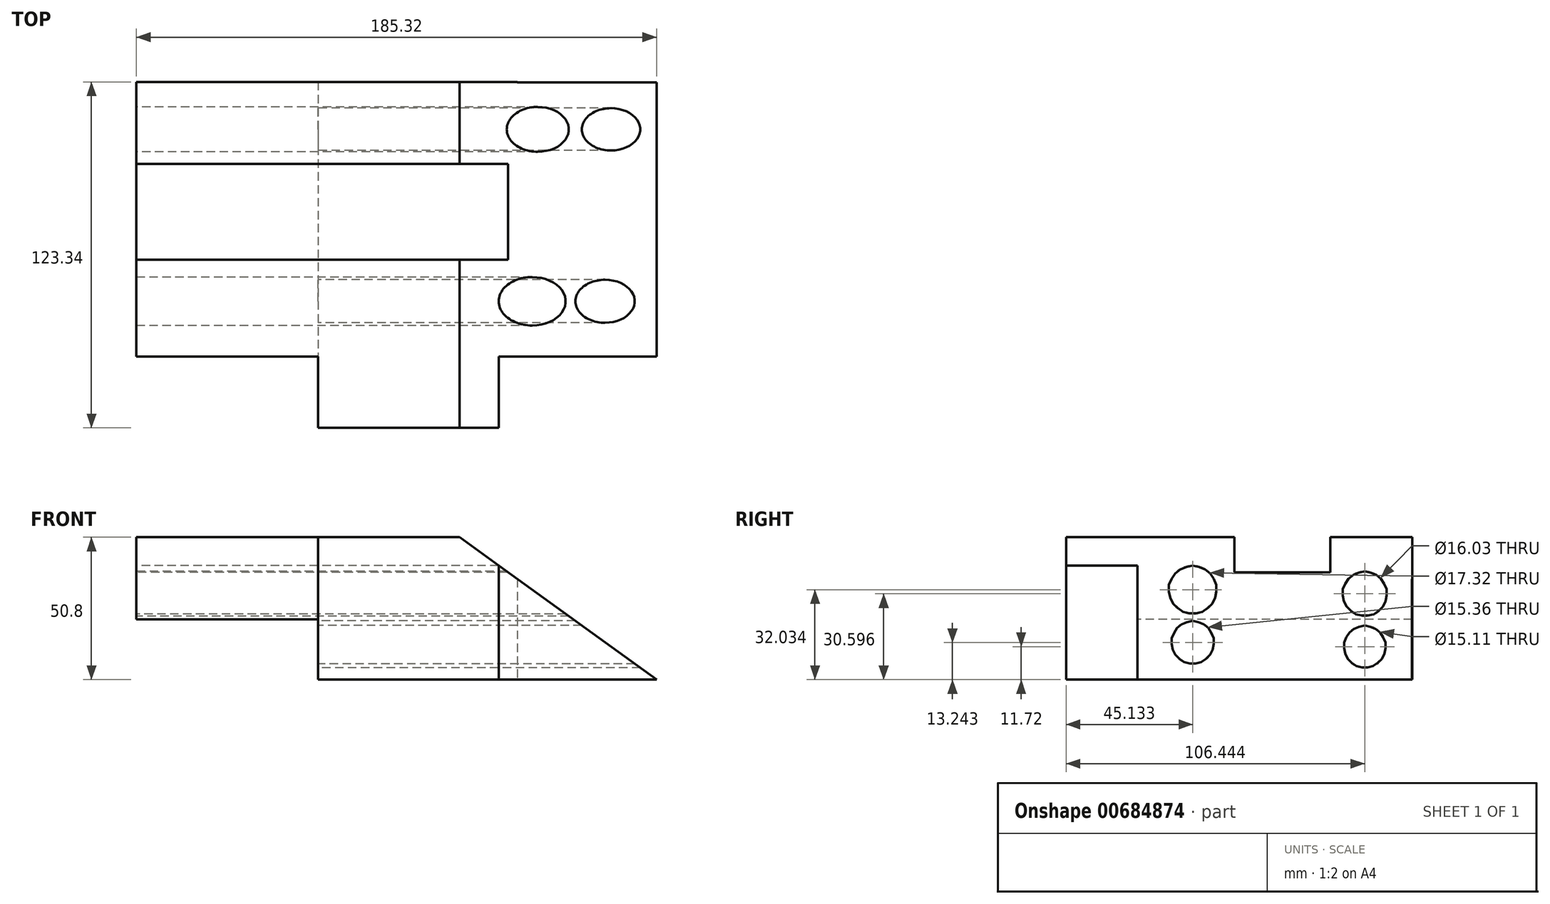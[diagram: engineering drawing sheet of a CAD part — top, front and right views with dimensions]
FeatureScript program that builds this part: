
annotation { "Feature Type Name" : "Feature", "Feature Type Description" : "" }
export const myFeature = defineFeature(function(context is Context, id is Id, definition is map)
    precondition{}
    {
        {
            var Q0;
            Q0=qCreatedBy(makeId("Top.planeOp"),FACE);
            var sketch = newSketch(context, id + "F0", { "sketchPlane" : qUnion([Q0])});
            skLineSegment(sketch, "E0.bottom", {"start": v(-58.71, -23.67) * mm, "end": v(125.79, -23.67) * mm});
            skLineSegment(sketch, "E0.top", {"start": v(-58.71, 74.27) * mm, "end": v(125.79, 74.27) * mm});
            skLineSegment(sketch, "E0.left", {"start": v(-58.71, -23.67) * mm, "end": v(-58.71, 74.27) * mm});
            skLineSegment(sketch, "E0.right", {"start": v(125.79, -23.67) * mm, "end": v(125.79, 74.27) * mm});
            skSolve(sketch);
        }
        {
            var Q0;
            Q0=makeQuery(id+"F0.imprint","IMPRINT",FACE,{"disambiguationData":[TD([[makeQuery(id+"F0.imprint","IMPRINT",EDGE,{"derivedFrom":sQuery(id+"F0.wireOp",EDGE,"E0.bottom")}),1.0]])]});
            extrude(context, id + "F1", {"entities" : qUnion([Q0]), "depth" : 50.8 * mm, "offsetDistance" : 25.4 * mm});
        }
        {
            var Q0;
            Q0=makeQuery(id+"F1.opExtrude","CAP_FACE",FACE,{"disambiguationData":[OSD([sQuery(id+"F0.wireOp",EDGE,"E0.bottom"),sQuery(id+"F0.wireOp",EDGE,"E0.top"),sQuery(id+"F0.wireOp",EDGE,"E0.left"),sQuery(id+"F0.wireOp",EDGE,"E0.right")])],"isStart":false});
            var sketch = newSketch(context, id + "F2", { "sketchPlane" : qUnion([Q0])});
            skLineSegment(sketch, "E1.bottom", {"start": v(125.79, -23.67) * mm, "end": v(77.04, -23.67) * mm});
            skLineSegment(sketch, "E1.top", {"start": v(125.79, 8.5) * mm, "end": v(77.04, 8.5) * mm});
            skLineSegment(sketch, "E1.left", {"start": v(125.79, -23.67) * mm, "end": v(125.79, 8.5) * mm});
            skLineSegment(sketch, "E1.right", {"start": v(77.04, -23.67) * mm, "end": v(77.04, 8.5) * mm});
            skSolve(sketch);
        }
        {
            var Q0;
            Q0 = qSketchRegion(id + "F2", true);
            extrude(context, id + "F3", {"entities" : qUnion([Q0]), "operationType" : NewBodyOperationType.REMOVE, "oppositeDirection" : true, "depth" : 51.82 * mm, "offsetDistance" : 25.4 * mm});
        }
        {
            var Q0;
            Q0=makeQuery(id+"F1.opExtrude","SWEPT_FACE",FACE,{"disambiguationData":[OSD([sQuery(id+"F0.wireOp",EDGE,"E0.bottom")])]});
            var sketch = newSketch(context, id + "F4", { "sketchPlane" : qUnion([Q0])});
            skLineSegment(sketch, "E2", {"start": v(56.37, 50.8) * mm, "end": v(126.6, 0) * mm});
            skLineSegment(sketch, "E3", {"start": v(126.6, 0) * mm, "end": v(54.95, 0) * mm});
            skLineSegment(sketch, "E4", {"start": v(54.95, 0) * mm, "end": v(56.37, 50.8) * mm});
            skSolve(sketch);
        }
        {
            var Q0;
            Q0=makeQuery(id+"F3.boolean.opBoolean","COPY",FACE,{"derivedFrom":makeQuery(id+"F3.opExtrude","SWEPT_FACE",FACE,{"disambiguationData":[OSD([sQuery(id+"F2.wireOp",EDGE,"E1.top")])]})});
            extrude(context, id + "F5", {"entities" : qUnion([Q0]), "operationType" : NewBodyOperationType.REMOVE, "oppositeDirection" : true, "depth" : 152.4 * mm, "offsetDistance" : 25.4 * mm});
        }
        {
            var Q0;
            {var subQ0=sQuery(id+"F4.wireOp",EDGE,"E3");var subQ1=sQuery(id+"F4.wireOp",EDGE,"E2");var subQ2=makeQuery(id+"F4.imprint","INTERSECT",VERTEX,{"derivedFrom":[subQ1,subQ0]});Q0=makeQuery(id+"F4.imprint","IMPRINT",FACE,{"disambiguationData":[TD([[makeQuery(id+"F4.imprint","IMPRINT",EDGE,{"disambiguationData":[TD([[subQ2,1.0]])],"derivedFrom":subQ1}),-1.0]])]});}
            extrude(context, id + "F6", {"entities" : qUnion([Q0]), "operationType" : NewBodyOperationType.ADD, "oppositeDirection" : true, "depth" : 97.8 * mm, "offsetDistance" : 25.4 * mm});
        }
        {
            var Q0;
            {var subQ0=sQuery(id+"F0.wireOp",EDGE,"E0.bottom");Q0=makeQuery(id+"F6.boolean.opBoolean","MERGE",FACE,{"derivedFrom":[makeQuery(id+"F1.opExtrude","SWEPT_FACE",FACE,{"disambiguationData":[OSD([subQ0])]}),makeQuery(id+"F6.opExtrude","CAP_FACE",FACE,{"disambiguationData":[OSD([subQ0,sQuery(id+"F2.wireOp",EDGE,"E1.bottom"),sQuery(id+"F2.wireOp",EDGE,"E1.right"),sQuery(id+"F4.wireOp",EDGE,"E2"),sQuery(id+"F4.wireOp",EDGE,"E3")])],"isStart":true})]});}
            var sketch = newSketch(context, id + "F7", { "sketchPlane" : qUnion([Q0])});
            skLineSegment(sketch, "E5", {"start": v(77.04, 35.85) * mm, "end": v(56.37, 50.8) * mm});
            skSolve(sketch);
        }
        {
            var Q0;
            {var subQ0=sQuery(id+"F7.wireOp",EDGE,"E5");Q0=makeQuery(id+"F7.imprint","IMPRINT",FACE,{"disambiguationData":[TD([[makeQuery(id+"F7.imprint","IMPRINT",EDGE,{"derivedFrom":subQ0}),-1.0]])]});}
            extrude(context, id + "F8", {"entities" : qUnion([Q0]), "operationType" : NewBodyOperationType.REMOVE, "oppositeDirection" : true, "depth" : 200.9 * mm, "offsetDistance" : 25.4 * mm});
        }
        {
            var Q0;
            {var subQ0=sQuery(id+"F0.wireOp",EDGE,"E0.bottom");Q0=makeQuery(id+"F6.boolean.opBoolean","MERGE",FACE,{"derivedFrom":[makeQuery(id+"F1.opExtrude","SWEPT_FACE",FACE,{"disambiguationData":[OSD([subQ0])]}),makeQuery(id+"F6.opExtrude","CAP_FACE",FACE,{"disambiguationData":[OSD([subQ0,sQuery(id+"F2.wireOp",EDGE,"E1.bottom"),sQuery(id+"F2.wireOp",EDGE,"E1.right"),sQuery(id+"F4.wireOp",EDGE,"E2"),sQuery(id+"F4.wireOp",EDGE,"E3")])],"isStart":true})]});}
            var sketch = newSketch(context, id + "F9", { "sketchPlane" : qUnion([Q0])});
            skLineSegment(sketch, "E6.bottom", {"start": v(-58.71, 0) * mm, "end": v(5.95, 0) * mm});
            skLineSegment(sketch, "E6.top", {"start": v(-58.71, 21.53) * mm, "end": v(5.95, 21.53) * mm});
            skLineSegment(sketch, "E6.left", {"start": v(-58.71, 0) * mm, "end": v(-58.71, 21.53) * mm});
            skLineSegment(sketch, "E6.right", {"start": v(5.95, 0) * mm, "end": v(5.95, 21.53) * mm});
            skSolve(sketch);
        }
        {
            var Q0;
            Q0=makeQuery(id+"F9.imprint","IMPRINT",FACE,{"disambiguationData":[TD([[makeQuery(id+"F9.imprint","IMPRINT",EDGE,{"derivedFrom":sQuery(id+"F9.wireOp",EDGE,"E6.bottom")}),1.0]])]});
            extrude(context, id + "F10", {"entities" : qUnion([Q0]), "operationType" : NewBodyOperationType.REMOVE, "oppositeDirection" : true, "depth" : 2540 * mm, "offsetDistance" : 25.4 * mm});
        }
        {
            var Q0;
            {var subQ0=sQuery(id+"F0.wireOp",EDGE,"E0.bottom");Q0=makeQuery(id+"F6.boolean.opBoolean","MERGE",FACE,{"derivedFrom":[makeQuery(id+"F1.opExtrude","SWEPT_FACE",FACE,{"disambiguationData":[OSD([subQ0])]}),makeQuery(id+"F6.opExtrude","CAP_FACE",FACE,{"disambiguationData":[OSD([subQ0,sQuery(id+"F2.wireOp",EDGE,"E1.bottom"),sQuery(id+"F2.wireOp",EDGE,"E1.right"),sQuery(id+"F4.wireOp",EDGE,"E2"),sQuery(id+"F4.wireOp",EDGE,"E3")])],"isStart":true})]});}
            var sketch = newSketch(context, id + "F11", { "sketchPlane" : qUnion([Q0])});
            skLineSegment(sketch, "E7", {"start": v(5.95, 0) * mm, "end": v(5.95, 50.8) * mm});
            skLineSegment(sketch, "E8", {"start": v(5.95, 50.8) * mm, "end": v(56.37, 50.8) * mm});
            skLineSegment(sketch, "E9", {"start": v(56.37, 50.8) * mm, "end": v(70.44, 40.63) * mm});
            skLineSegment(sketch, "E10", {"start": v(70.44, 40.63) * mm, "end": v(70.44, 0) * mm});
            skLineSegment(sketch, "E11", {"start": v(70.44, 0) * mm, "end": v(5.95, 0) * mm});
            skSolve(sketch);
        }
        {
            var Q0;
            {var subQ0=sQuery(id+"F11.wireOp",EDGE,"E8");Q0=makeQuery(id+"F11.imprint","IMPRINT",FACE,{"disambiguationData":[TD([[makeQuery(id+"F11.imprint","IMPRINT",EDGE,{"derivedFrom":subQ0}),-1.0]])]});}
            extrude(context, id + "F12", {"entities" : qUnion([Q0]), "operationType" : NewBodyOperationType.ADD, "depth" : 25.4 * mm, "offsetDistance" : 25.4 * mm});
        }
        {
            var Q0;
            Q0=makeQuery(id+"F1.opExtrude","SWEPT_FACE",FACE,{"disambiguationData":[OSD([sQuery(id+"F0.wireOp",EDGE,"E0.left")])]});
            var sketch = newSketch(context, id + "F13", { "sketchPlane" : qUnion([Q0])});
            skLineSegment(sketch, "E12.bottom", {"start": v(-45.03, 50.8) * mm, "end": v(-10.87, 50.8) * mm});
            skLineSegment(sketch, "E12.top", {"start": v(-45.03, 38.3) * mm, "end": v(-10.87, 38.3) * mm});
            skLineSegment(sketch, "E12.left", {"start": v(-45.03, 50.8) * mm, "end": v(-45.03, 38.3) * mm});
            skLineSegment(sketch, "E12.right", {"start": v(-10.87, 50.8) * mm, "end": v(-10.87, 38.3) * mm});
            skSolve(sketch);
        }
        {
            var Q0;
            Q0=makeQuery(id+"F13.imprint","IMPRINT",FACE,{"disambiguationData":[TD([[makeQuery(id+"F13.imprint","IMPRINT",EDGE,{"derivedFrom":sQuery(id+"F13.wireOp",EDGE,"E12.bottom")}),1.0]])]});
            extrude(context, id + "F14", {"entities" : qUnion([Q0]), "operationType" : NewBodyOperationType.REMOVE, "oppositeDirection" : true, "depth" : 177.8 * mm, "offsetDistance" : 25.4 * mm});
        }
        {
            var Q0;
            Q0=makeQuery(id+"F1.opExtrude","SWEPT_FACE",FACE,{"disambiguationData":[OSD([sQuery(id+"F0.wireOp",EDGE,"E0.left")])]});
            var sketch = newSketch(context, id + "F15", { "sketchPlane" : qUnion([Q0])});
            skCircle(sketch, "E13", {"center": v(3.94, 32.03) * mm, "radius": 8.66 * mm});
            skCircle(sketch, "E14", {"center": v(-57.37, 30.6) * mm, "radius": 8.01 * mm});
            skCircle(sketch, "E15", {"center": v(-57.37, 11.72) * mm, "radius": 7.56 * mm});
            skCircle(sketch, "E16", {"center": v(3.94, 13.24) * mm, "radius": 7.68 * mm});
            skSolve(sketch);
        }
        {
            var Q0;
            Q0=makeQuery(id+"F15.imprint","IMPRINT",FACE,{"disambiguationData":[TD([[makeQuery(id+"F15.imprint","IMPRINT",EDGE,{"derivedFrom":sQuery(id+"F15.wireOp",EDGE,"E14")}),1.0]])]});
            extrude(context, id + "F16", {"entities" : qUnion([Q0]), "operationType" : NewBodyOperationType.REMOVE, "oppositeDirection" : true, "depth" : 381 * mm, "offsetDistance" : 25.4 * mm});
        }
        {
            var Q0;
            Q0=makeQuery(id+"F15.imprint","IMPRINT",FACE,{"disambiguationData":[TD([[makeQuery(id+"F15.imprint","IMPRINT",EDGE,{"derivedFrom":sQuery(id+"F15.wireOp",EDGE,"E13")}),1.0]])]});
            extrude(context, id + "F17", {"entities" : qUnion([Q0]), "operationType" : NewBodyOperationType.REMOVE, "oppositeDirection" : true, "depth" : 381 * mm, "offsetDistance" : 25.4 * mm});
        }
        {
            var Q0;
            Q0=makeQuery(id+"F15.imprint","IMPRINT",FACE,{"disambiguationData":[TD([[makeQuery(id+"F15.imprint","IMPRINT",EDGE,{"derivedFrom":sQuery(id+"F15.wireOp",EDGE,"E16")}),1.0]])]});
            extrude(context, id + "F18", {"entities" : qUnion([Q0]), "operationType" : NewBodyOperationType.REMOVE, "oppositeDirection" : true, "depth" : 381 * mm, "offsetDistance" : 25.4 * mm});
        }
        {
            var Q0;
            Q0=makeQuery(id+"F15.imprint","IMPRINT",FACE,{"disambiguationData":[TD([[makeQuery(id+"F15.imprint","IMPRINT",EDGE,{"derivedFrom":sQuery(id+"F15.wireOp",EDGE,"E15")}),1.0]])]});
            extrude(context, id + "F19", {"entities" : qUnion([Q0]), "operationType" : NewBodyOperationType.REMOVE, "oppositeDirection" : true, "depth" : 381 * mm, "offsetDistance" : 25.4 * mm});
        }
    });
